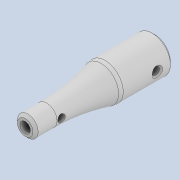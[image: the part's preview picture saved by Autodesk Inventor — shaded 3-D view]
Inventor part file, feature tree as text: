
AUTODESK INVENTOR PART (.ipt)
format: ipt  version: 2020 (Build 240168000, 168)  size: 218,624 bytes
history: native  units: mm
features: extrude x6, sketch x6, chamfer x4, other x3, fillet x2, projected_geometry x2, reference x1
ambient origin geometry x8: Origin, YZ Plane, XZ Plane, XY Plane, X Axis, Y Axis, Z Axis, Center Point
bodies: Solid1 (feature_tree)
feature tree (24):
  extrude  "Extrusion1"  Depth=7.0mm
  extrude  "Extrusion2"  Depth=2.0mm TaperAngle=0.0deg
  extrude  "Extrusion3"  Depth=4.0mm
  fillet  "Fillet1"  Radius=15.0mm
  fillet  "Fillet2"  Radius=40.0mm
  chamfer  "Chamfer1"  Distance=0.5mm Angle=45.0deg
  chamfer  "Chamfer2"  Distance=0.5mm Angle=45.0deg
  extrude  "Extrusion4"  Depth=1.4mm
  chamfer  "Chamfer3"  Distance=15.0mm
  chamfer  "Chamfer4"  Distance=0.3mm Angle=45.0deg
  extrude  "Extrusion5"  Depth=10.0mm
  extrude  "Extrusion6"  Depth=10.0mm TaperAngle=0.0deg
  sketch  "Sketch1"  dims[d0=3.0mm d1=7.0mm]
  reference  "Reference1"
  sketch  "Sketch2"  dims[d2=8.0mm d3=0.0mm d4=2.0mm d5=0.0mm]
  sketch  "Sketch3"  dims[d6=2.0mm d7=4.0mm d8=15.0mm d9=0.0mm d10=40.0mm]
  projected_geometry  "Projected Loop1"
  sketch  "Sketch4"  dims[d11=3.0mm d12=0.5mm d13=2.0mm d14=45.0deg d15=0.5mm d16=2.0mm d17=45.0deg]
  sketch  "Sketch5"  dims[d18=3.0mm d19=1.4mm d20=15.0mm d21=0.0mm d22=0.3mm d23=2.0mm d24=45.0deg]
  projected_geometry  "Projected Loop2"
  sketch  "Sketch6"  dims[d25=0.5mm d26=2.0mm d27=45.0deg d28=2.0mm d29=10.0mm d30=0.0mm d31=5.0mm d32=1.4mm d33=10.0mm d34=0.0mm]
  parser-record x1  (decoder bookkeeping rows leaked as tree rows — omitted from the tree; the rows remain in map.json)
  other  "tip_ass_t1.iam"
  other  "pin_3_30:1"
note: 1 file-system path scrubbed to <path> (originals preserved in map.json)
